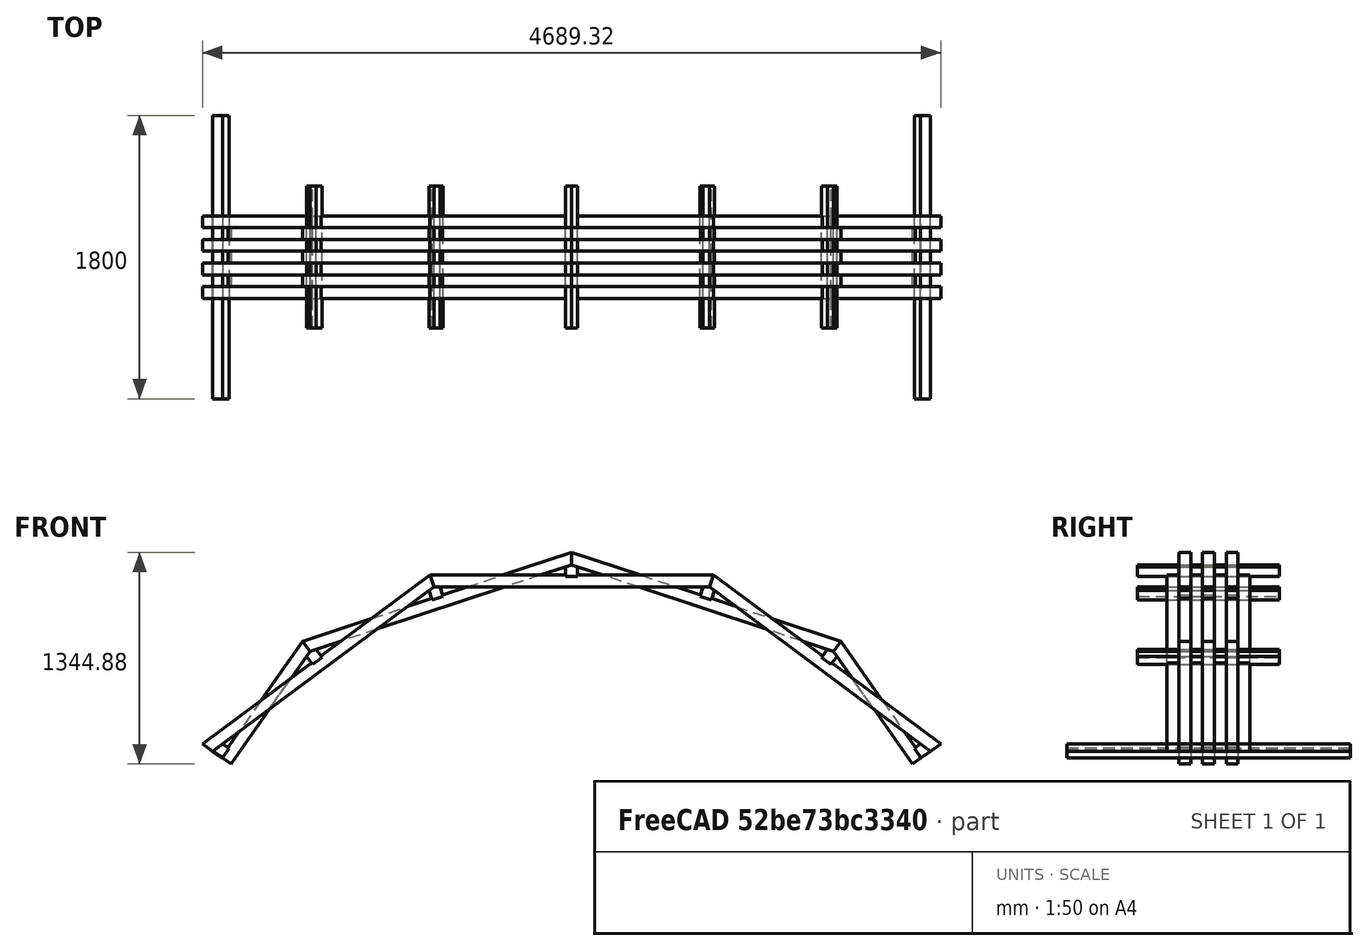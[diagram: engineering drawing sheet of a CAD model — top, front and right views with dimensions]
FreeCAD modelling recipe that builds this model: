
FCSTD DOCUMENT  (FreeCAD 0.18R4 (GitTag))
Label: bridge
License: Public Domain
LicenseURL: http://en.wikipedia.org/wiki/Public_domain
objects: Part::Feature×13, Part::Compound×9
note: 22 computed .brp shape members not serialized (recipe doc carries the construction recipe); baked Part::Feature solids carry a one-line shape summary decoded from their .brp

FEATURE [Part::Feature] Deck_Piece001 .. Deck_Piece004  x4 (patterned run collapsed; names and placements below)
  shape: bbox 1800 x 75 x 75 mm, 10 faces (baked)
  placements: 4 in arithmetic series — first pos=(0,-300,0) rot=(0,0,1;0rad), step (0,150,0), last pos=(0,150,0) rot=(0,0,1;0rad)
FEATURE [Part::Feature] Cross_Piece001
  Placement = pos=(0,-487.5,0) rot=(0,0,1;0rad)
  shape: bbox 75 x 900 x 75 mm, 7 faces (baked)
FEATURE [Part::Compound] Compound  label="Even_Assembly1"
  Links = -> [Deck_Piece001,Deck_Piece003,Cross_Piece001,Deck_Piece002,Deck_Piece004]
FEATURE [Part::Feature] Deck_Piece005
  Placement = pos=(0,-225,0) rot=(0,0,1;0rad)
  shape: bbox 1800 x 75 x 75 mm, 10 faces (baked)
FEATURE [Part::Feature] Deck_Piece006
  Placement = pos=(0,-75,0) rot=(0,0,1;0rad)
  shape: bbox 1800 x 75 x 75 mm, 10 faces (baked)
FEATURE [Part::Feature] Deck_Piece007
  Placement = pos=(0,75,0) rot=(0,0,1;0rad)
  shape: bbox 1800 x 75 x 75 mm, 10 faces (baked)
FEATURE [Part::Feature] Cross_Piece002
  Placement = pos=(0,-487.5,0) rot=(0,0,1;0rad)
  shape: bbox 75 x 900 x 75 mm, 7 faces (baked)
FEATURE [Part::Compound] Compound001  label="Odd_Assembly1"
  Links = -> [Deck_Piece005,Deck_Piece006,Cross_Piece002,Deck_Piece007]
  Placement = pos=(0,0,0) rot=(0,1,0;0.319471rad)
FEATURE [Part::Compound] Compound002  label="Odd_Assembly2"
  Links = -> [Deck_Piece005,Deck_Piece006,Cross_Piece002,Deck_Piece007]
  Placement = pos=(0,0,0) rot=(0,-1,0;0.319395rad)
FEATURE [Part::Compound] Compound003  label="Even_Assembly2"
  Links = -> [Deck_Piece001,Deck_Piece003,Cross_Piece001,Deck_Piece002,Deck_Piece004]
  Placement = pos=(0,0,0) rot=(0,1,0;0.638791rad)
FEATURE [Part::Compound] Compound004  label="Even_Assembly3"
  Links = -> [Deck_Piece001,Deck_Piece003,Cross_Piece001,Deck_Piece002,Deck_Piece004]
  Placement = pos=(0,0,0) rot=(0,-1,0;0.638791rad)
FEATURE [Part::Compound] Compound005  label="Main_Span"
  Links = -> [Compound,Compound004,Compound001,Compound002,Compound003]
FEATURE [Part::Feature] End_Piece
  Placement = pos=(0,-487.5,0) rot=(0,0,1;0rad)
  shape: bbox 75 x 1800 x 75 mm, 6 faces (baked)
FEATURE [Part::Feature] End_Deck001
  Placement = pos=(0,225,0) rot=(0,0,1;0rad)
  shape: bbox 900 x 75 x 75 mm, 8 faces (baked)
FEATURE [Part::Feature] End_Deck002
  Placement = pos=(0,375,0) rot=(0,0,1;0rad)
  shape: bbox 900 x 75 x 75 mm, 8 faces (baked)
FEATURE [Part::Feature] End_Deck003
  Placement = pos=(0,525,0) rot=(0,0,1;0rad)
  shape: bbox 900 x 75 x 75 mm, 8 faces (baked)
FEATURE [Part::Compound] Compound006  label="Right_End_Assembly"
  Links = -> [End_Deck001,End_Deck003,End_Deck002,End_Piece]
  Placement = pos=(0,-450,0) rot=(0,1,0;0.958412rad)
FEATURE [Part::Compound] Compound007  label="Left_End_Assembly"
  Links = -> [End_Deck001,End_Deck003,End_Deck002,End_Piece]
  Placement = pos=(4.6e-14,375,0) rot=(-0.460974,0,0.887413;3.14159rad)
FEATURE [Part::Compound] Compound008  label="Bridge"
  Links = -> [Compound005,Compound007,Compound006]
